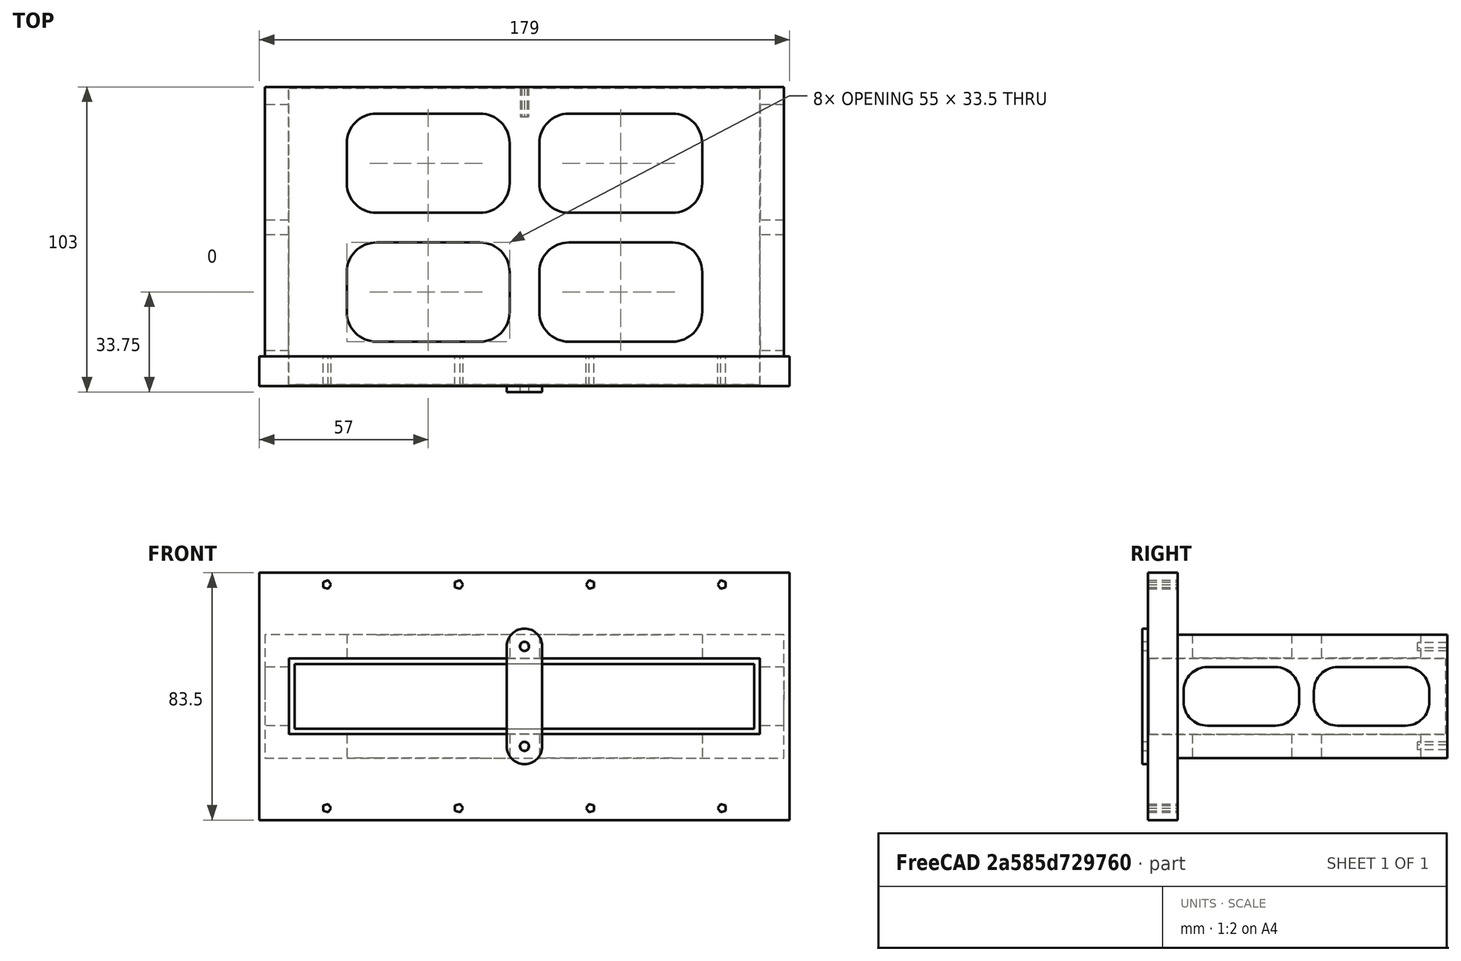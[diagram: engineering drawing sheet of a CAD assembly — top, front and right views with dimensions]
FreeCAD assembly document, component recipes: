
FREECAD ASSEMBLY — COMPONENT RECIPES ("tplink-er605")

This assembly document has 3 components, labeled P0..P2 below (a component is one placed body or linked part). 3 of them carry a construction recipe — the FreeCAD feature program that regenerates the part from scratch, quoted from this document or its linked companion documents; the rest are supplied as boundary geometry only. No exploded tour is included for this assembly.
COMPONENT P0 — recipe-attached ("ER605", modeled in this document).
Construction recipe (the document's own serialized feature program — sketch geometry with constraints, then the solid features built on it; lengths are millimeters unless a unit is written):

FEATURE [PartDesign::Plane] DatumPlane006  label="ER605 Front"
  Length = 176.833
  MapMode = 5
  Placement = pos=(0,0,0) rot=(1,0,0;1.5708rad)
  ResizeMode = 0
  Support = -> [XZ_Plane004]
  Width = 67.8326
FEATURE [PartDesign::Plane] DatumPlane007  label="ER605 Back"
  AttachmentOffset = pos=(0,0,-100.5) rot=(0,0,1;0rad)
  Length = 176.833
  MapMode = 5
  Placement = pos=(0,100.5,2.23e-14) rot=(1,0,0;1.5708rad)
  ResizeMode = 0
  Support = -> [DatumPlane006]
  Width = 67.8326
FEATURE [Sketcher::SketchObject] Sketch008  label="ER605 Front Profile"
  FullyConstrained = true
  MapMode = 5
  Placement = pos=(0,0,0) rot=(1,0,0;1.5708rad)
  Support = -> [DatumPlane006]
  sketch-geometry (5):
    g0: LineSegment StartX=-79.5 StartY=12.75 StartZ=0 EndX=-79.5 EndY=-12.75 EndZ=0
    g1: LineSegment StartX=-79.5 StartY=-12.75 StartZ=0 EndX=79.5 EndY=-12.75 EndZ=0
    g2: LineSegment StartX=79.5 StartY=-12.75 StartZ=0 EndX=79.5 EndY=12.75 EndZ=0
    g3: LineSegment StartX=79.5 StartY=12.75 StartZ=0 EndX=-79.5 EndY=12.75 EndZ=0
    g4: GeomPoint X=0 Y=0 Z=0
  constraints (12):
    c: Coincident(g0,g1)
    c: Coincident(g1,g2)
    c: Coincident(g2,g3)
    c: Coincident(g3,g0)
    c: Horizontal(g1)
    c: Horizontal(g3)
    c: Vertical(g0)
    c: Vertical(g2)
    c: Symmetric(g1,g0,g4)
    c: Coincident(g4,g-1)
    c: DistanceX(g3,g3) = 159  'width'
    c: DistanceY(g2,g2) = 25.5  'height'
FEATURE [PartDesign::Pad] Pad002  label="ER605 Volume"
  Direction = (0,-1,-2e-16)
  Length = 10
  Length2 = 10
  Placement = pos=(0,0,0) rot=(1,0,0;1.5708rad)
  Profile = -> Sketch008
  ReferenceAxis = -> Sketch008 [N_Axis]
  Type = 3
  UpToFace = -> DatumPlane007 [Plane]
FEATURE [PartDesign::Body] ER605_Body  label="ER605 Body"
  Group = -> [DatumPlane006,DatumPlane007,Sketch008,Pad002]
  Origin = -> Origin004
  Tip = -> Pad002
COMPONENT P1 — recipe-attached ("Rack Mount", modeled in this document).
Construction recipe (the document's own serialized feature program — sketch geometry with constraints, then the solid features built on it; lengths are millimeters unless a unit is written):

FEATURE [PartDesign::Plane] DatumPlane  label="Front Panel Front"
  Length = 203.451
  MapMode = 5
  Placement = pos=(0,0,0) rot=(1,0,0;1.5708rad)
  ResizeMode = 0
  Support = -> [XZ_Plane]
  Width = 107.951
FEATURE [PartDesign::Plane] DatumPlane002  label="Front Panel Back"
  AttachmentOffset = pos=(0,0,-10) rot=(0,0,1;0rad)
  Length = 203.451
  MapMode = 5
  Placement = pos=(0,10,2.2e-15) rot=(1,0,0;1.5708rad)
  ResizeMode = 0
  Support = -> [DatumPlane]
  Width = 107.951
FEATURE [Sketcher::SketchObject] Sketch  label="Front Panel Outer"
  FullyConstrained = true
  MapMode = 5
  Placement = pos=(0,0,0) rot=(1,0,0;1.5708rad)
  Support = -> [DatumPlane]
  sketch-geometry (5):
    g0: LineSegment StartX=-89.5 StartY=41.75 StartZ=0 EndX=-89.5 EndY=-41.75 EndZ=0
    g1: LineSegment StartX=-89.5 StartY=-41.75 StartZ=0 EndX=89.5 EndY=-41.75 EndZ=0
    g2: LineSegment StartX=89.5 StartY=-41.75 StartZ=0 EndX=89.5 EndY=41.75 EndZ=0
    g3: LineSegment StartX=89.5 StartY=41.75 StartZ=0 EndX=-89.5 EndY=41.75 EndZ=0
    g4: GeomPoint X=0 Y=0 Z=0
  constraints (12):
    c: Coincident(g0,g1)
    c: Coincident(g1,g2)
    c: Coincident(g2,g3)
    c: Coincident(g3,g0)
    c: Horizontal(g1)
    c: Horizontal(g3)
    c: Vertical(g0)
    c: Vertical(g2)
    c: Symmetric(g1,g0,g4)
    c: Coincident(g4,g-1)
    c: DistanceX(g3,g3) = 179  'width'
    c: DistanceY(g2,g2) = 83.5  'height'
FEATURE [PartDesign::Pad] Pad  label="Front Panel"
  Direction = (0,-1,-2e-16)
  Length = 10
  Length2 = 10
  Placement = pos=(0,0,0) rot=(1,0,0;1.5708rad)
  Profile = -> Sketch
  ReferenceAxis = -> Sketch [N_Axis]
  Type = 3
  UpToFace = -> DatumPlane002 [Plane]
FEATURE [Sketcher::SketchObject] Sketch002  label="Front Panel Mounting Holes Outer"
  FullyConstrained = true
  MapMode = 5
  Placement = pos=(0,0,0) rot=(1,0,0;1.5708rad)
  Support = -> [DatumPlane]
  sketch-geometry (51):
    g0: LineSegment StartX=-66.75 StartY=37.75 StartZ=0 EndX=66.75 EndY=37.75 EndZ=0
    g1: LineSegment StartX=0 StartY=37.75 StartZ=0 EndX=0 EndY=-37.75 EndZ=0
    g2: LineSegment StartX=23.4635 StartY=38.6317 StartZ=0 EndX=21.7865 EndY=39.1766 EndZ=0
    g3: LineSegment StartX=21.7865 StartY=39.1766 StartZ=0 EndX=20.75 EndY=37.75 EndZ=0
    g4: LineSegment StartX=20.75 StartY=37.75 StartZ=0 EndX=21.7865 EndY=36.3234 EndZ=0
    g5: LineSegment StartX=21.7865 StartY=36.3234 StartZ=0 EndX=23.4635 EndY=36.8683 EndZ=0
    g6: LineSegment StartX=23.4635 StartY=36.8683 StartZ=0 EndX=23.4635 EndY=38.6317 EndZ=0
    g7: Circle CenterX=22.25 CenterY=37.75 CenterZ=0 NormalX=0 NormalY=0 NormalZ=1 AngleXU=0 Radius=1.5
    g8: LineSegment StartX=67.9635 StartY=36.8683 StartZ=0 EndX=67.9635 EndY=38.6317 EndZ=0
    g9: LineSegment StartX=67.9635 StartY=38.6317 StartZ=0 EndX=66.2865 EndY=39.1766 EndZ=0
    g10: LineSegment StartX=66.2865 StartY=39.1766 StartZ=0 EndX=65.25 EndY=37.75 EndZ=0
    g11: LineSegment StartX=65.25 StartY=37.75 StartZ=0 EndX=66.2865 EndY=36.3234 EndZ=0
    g12: LineSegment StartX=66.2865 StartY=36.3234 StartZ=0 EndX=67.9635 EndY=36.8683 EndZ=0
    g13: Circle CenterX=66.75 CenterY=37.75 CenterZ=0 NormalX=0 NormalY=0 NormalZ=1 AngleXU=0 Radius=1.5
    g14: LineSegment StartX=-20.75 StartY=37.75 StartZ=0 EndX=-21.7865 EndY=39.1766 EndZ=0
    g15: LineSegment StartX=-21.7865 StartY=39.1766 StartZ=0 EndX=-23.4635 EndY=38.6317 EndZ=0
    g16: LineSegment StartX=-23.4635 StartY=38.6317 StartZ=0 EndX=-23.4635 EndY=36.8683 EndZ=0
    g17: LineSegment StartX=-23.4635 StartY=36.8683 StartZ=0 EndX=-21.7865 EndY=36.3234 EndZ=0
    g18: LineSegment StartX=-21.7865 StartY=36.3234 StartZ=0 EndX=-20.75 EndY=37.75 EndZ=0
    g19: Circle CenterX=-22.25 CenterY=37.75 CenterZ=0 NormalX=0 NormalY=0 NormalZ=1 AngleXU=0 Radius=1.5
    g20: LineSegment StartX=-65.25 StartY=37.75 StartZ=0 EndX=-66.2865 EndY=39.1766 EndZ=0
    g21: LineSegment StartX=-66.2865 StartY=39.1766 StartZ=0 EndX=-67.9635 EndY=38.6317 EndZ=0
    g22: LineSegment StartX=-67.9635 StartY=38.6317 StartZ=0 EndX=-67.9635 EndY=36.8683 EndZ=0
    g23: LineSegment StartX=-67.9635 StartY=36.8683 StartZ=0 EndX=-66.2865 EndY=36.3234 EndZ=0
    g24: LineSegment StartX=-66.2865 StartY=36.3234 StartZ=0 EndX=-65.25 EndY=37.75 EndZ=0
    g25: Circle CenterX=-66.75 CenterY=37.75 CenterZ=0 NormalX=0 NormalY=0 NormalZ=1 AngleXU=0 Radius=1.5
    g26: LineSegment StartX=-66.2865 StartY=-39.1766 StartZ=0 EndX=-65.25 EndY=-37.75 EndZ=0
    g27: LineSegment StartX=-65.25 StartY=-37.75 StartZ=0 EndX=-66.2865 EndY=-36.3234 EndZ=0
    g28: LineSegment StartX=-66.2865 StartY=-36.3234 StartZ=0 EndX=-67.9635 EndY=-36.8683 EndZ=0
    g29: LineSegment StartX=-67.9635 StartY=-36.8683 StartZ=0 EndX=-67.9635 EndY=-38.6317 EndZ=0
    g30: LineSegment StartX=-67.9635 StartY=-38.6317 StartZ=0 EndX=-66.2865 EndY=-39.1766 EndZ=0
    g31: Circle CenterX=-66.75 CenterY=-37.75 CenterZ=0 NormalX=0 NormalY=0 NormalZ=1 AngleXU=0 Radius=1.5
    g32: LineSegment StartX=-20.75 StartY=-37.75 StartZ=0 EndX=-21.7865 EndY=-36.3234 EndZ=0
    g33: LineSegment StartX=-21.7865 StartY=-36.3234 StartZ=0 EndX=-23.4635 EndY=-36.8683 EndZ=0
    g34: LineSegment StartX=-23.4635 StartY=-36.8683 StartZ=0 EndX=-23.4635 EndY=-38.6317 EndZ=0
    g35: LineSegment StartX=-23.4635 StartY=-38.6317 StartZ=0 EndX=-21.7865 EndY=-39.1766 EndZ=0
    g36: LineSegment StartX=-21.7865 StartY=-39.1766 StartZ=0 EndX=-20.75 EndY=-37.75 EndZ=0
    g37: Circle CenterX=-22.25 CenterY=-37.75 CenterZ=0 NormalX=0 NormalY=0 NormalZ=1 AngleXU=0 Radius=1.5
    g38: LineSegment StartX=21.7865 StartY=-39.1766 StartZ=0 EndX=23.4635 EndY=-38.6317 EndZ=0
    g39: LineSegment StartX=23.4635 StartY=-38.6317 StartZ=0 EndX=23.4635 EndY=-36.8683 EndZ=0
    g40: LineSegment StartX=23.4635 StartY=-36.8683 StartZ=0 EndX=21.7865 EndY=-36.3234 EndZ=0
    g41: LineSegment StartX=21.7865 StartY=-36.3234 StartZ=0 EndX=20.75 EndY=-37.75 EndZ=0
    g42: LineSegment StartX=20.75 StartY=-37.75 StartZ=0 EndX=21.7865 EndY=-39.1766 EndZ=0
    g43: Circle CenterX=22.25 CenterY=-37.75 CenterZ=0 NormalX=0 NormalY=0 NormalZ=1 AngleXU=0 Radius=1.5
    g44: LineSegment StartX=67.9635 StartY=-36.8683 StartZ=0 EndX=66.2865 EndY=-36.3234 EndZ=0
    g45: LineSegment StartX=66.2865 StartY=-36.3234 StartZ=0 EndX=65.25 EndY=-37.75 EndZ=0
    g46: LineSegment StartX=65.25 StartY=-37.75 StartZ=0 EndX=66.2865 EndY=-39.1766 EndZ=0
    g47: LineSegment StartX=66.2865 StartY=-39.1766 StartZ=0 EndX=67.9635 EndY=-38.6317 EndZ=0
    g48: LineSegment StartX=67.9635 StartY=-38.6317 StartZ=0 EndX=67.9635 EndY=-36.8683 EndZ=0
    g49: Circle CenterX=66.75 CenterY=-37.75 CenterZ=0 NormalX=0 NormalY=0 NormalZ=1 AngleXU=0 Radius=1.5
    g50: LineSegment StartX=-66.75 StartY=-37.75 StartZ=0 EndX=66.75 EndY=-37.75 EndZ=0
  constraints (122):
    c: Horizontal(g0)
    c: PointOnObject(g1,g-2)
    c: Symmetric(g1,g1,g-1)
    c: DistanceY(g1,g1) = 75.5
    c: Symmetric(g0,g0,g1)
    c: Coincident(g2,g3)
    c: Coincident(g3,g4)
    c: Coincident(g4,g5)
    c: Coincident(g5,g6)
    c: Coincident(g6,g2)
    c: Equal(g2, g3-g6) x4
    c: PointOnObject(g2,g7)
    c: PointOnObject(g3,g7)
    c: PointOnObject(g4,g7)
    c: PointOnObject(g5,g7)
    c: PointOnObject(g6,g7)
    c: PointOnObject(g7,g0)
    c: Coincident(g8,g9)
    c: Coincident(g9,g10)
    c: Coincident(g10,g11)
    c: Coincident(g11,g12)
    c: Coincident(g12,g8)
    c: Equal(g8, g9-g12) x4
    c: PointOnObject(g8,g13)
    c: PointOnObject(g9,g13)
    c: PointOnObject(g10,g13)
    c: PointOnObject(g11,g13)
    c: PointOnObject(g12,g13)
    c: Coincident(g13,g0)
    c: Coincident(g14,g15)
    c: Coincident(g15,g16)
    c: Coincident(g16,g17)
    c: Coincident(g17,g18)
    c: Coincident(g18,g14)
    c: Equal(g14, g15-g18) x4
    c: PointOnObject(g14,g19)
    c: PointOnObject(g15,g19)
    c: PointOnObject(g16,g19)
    c: PointOnObject(g17,g19)
    c: PointOnObject(g18,g19)
    c: PointOnObject(g19,g0)
    c: Coincident(g20,g21)
    c: Coincident(g21,g22)
    c: Coincident(g22,g23)
    c: Coincident(g23,g24)
    c: Coincident(g24,g20)
    c: Equal(g20, g21-g24) x4
    c: PointOnObject(g20,g25)
    c: PointOnObject(g21,g25)
    c: PointOnObject(g22,g25)
    c: PointOnObject(g23,g25)
    c: PointOnObject(g24,g25)
    c: Coincident(g25,g0)
    c: DistanceX(g7,g0) = 44.5
    c: Equal(g7,g13)
    c: Equal(g19,g25)
    c: Coincident(g26,g27)
    c: Coincident(g27,g28)
    c: Coincident(g28,g29)
    c: Coincident(g29,g30)
    c: Coincident(g30,g26)
    c: Equal(g26, g27-g30) x4
    c: PointOnObject(g26,g31)
    c: PointOnObject(g27,g31)
    c: PointOnObject(g28,g31)
    c: PointOnObject(g29,g31)
    c: PointOnObject(g30,g31)
    c: Coincident(g32,g33)
    c: Coincident(g33,g34)
    c: Coincident(g34,g35)
    c: Coincident(g35,g36)
    c: Coincident(g36,g32)
    c: Equal(g32, g33-g36) x4
    c: PointOnObject(g32,g37)
    c: PointOnObject(g33,g37)
    c: PointOnObject(g34,g37)
    c: PointOnObject(g35,g37)
    c: PointOnObject(g36,g37)
    c: Coincident(g38,g39)
    c: Coincident(g39,g40)
    c: Coincident(g40,g41)
    c: Coincident(g41,g42)
    c: Coincident(g42,g38)
    c: Equal(g38, g39-g42) x4
    c: PointOnObject(g38,g43)
    c: PointOnObject(g39,g43)
    c: PointOnObject(g40,g43)
    c: PointOnObject(g41,g43)
    c: PointOnObject(g42,g43)
    c: Coincident(g44,g45)
    c: Coincident(g45,g46)
    c: Coincident(g46,g47)
    c: Coincident(g47,g48)
    c: Coincident(g48,g44)
    c: Equal(g44, g45-g48) x4
    c: PointOnObject(g44,g49)
    c: PointOnObject(g45,g49)
    c: PointOnObject(g46,g49)
    c: PointOnObject(g47,g49)
    c: PointOnObject(g48,g49)
    c: Symmetric(g19,g37,g-1)
    c: Symmetric(g31,g0,g-1)
    c: Symmetric(g7,g43,g-1)
    c: Symmetric(g0,g49,g-1)
    c: Equal(g31,g37)
    c: Diameter(g13) = 3
    c: Equal(g31,g13)
    c: PointOnObject(g10,g0)
    c: PointOnObject(g3,g0)
    c: PointOnObject(g14,g0)
    c: PointOnObject(g20,g0)
    c: Coincident(g50,g31)
    c: Coincident(g50,g49)
    c: PointOnObject(g45,g50)
    c: PointOnObject(g41,g50)
    c: PointOnObject(g32,g50)
    c: PointOnObject(g26,g50)
    c: Equal(g19,g7)
    c: Equal(g13,g49)
    c: Equal(g49,g43)
    c: DistanceX(g19,g7) = 44.5
    c: DistanceX(g0,g19) = 44.5
FEATURE [PartDesign::Pocket] Pocket001  label="Front Panel Mounting Holes"
  BaseFeature = -> Pad
  Direction = (0,1,2e-16)
  Length = 0
  Length2 = 5
  Placement = pos=(0,0,0) rot=(1,0,0;1.5708rad)
  Profile = -> Sketch002
  ReferenceAxis = -> Sketch002 [N_Axis]
  Type = 3
  UpToFace = -> DatumPlane002
FEATURE [Sketcher::SketchObject] Sketch003  label="Front Panel Cutout Outer"
  FullyConstrained = true
  MapMode = 5
  Placement = pos=(0,0,0) rot=(1,0,0;1.5708rad)
  Support = -> [DatumPlane]
  expr: Constraints[10] = <<Device Cutout Outer>>.Constraints.height - 4 mm
  expr: Constraints[11] = <<Device Cutout Outer>>.Constraints.width - 4 mm
  sketch-geometry (5):
    g0: LineSegment StartX=-77.625 StartY=10.875 StartZ=0 EndX=-77.625 EndY=-10.875 EndZ=0
    g1: LineSegment StartX=-77.625 StartY=-10.875 StartZ=0 EndX=77.625 EndY=-10.875 EndZ=0
    g2: LineSegment StartX=77.625 StartY=-10.875 StartZ=0 EndX=77.625 EndY=10.875 EndZ=0
    g3: LineSegment StartX=77.625 StartY=10.875 StartZ=0 EndX=-77.625 EndY=10.875 EndZ=0
    g4: GeomPoint X=0 Y=0 Z=0
  constraints (12):
    c: Coincident(g0,g1)
    c: Coincident(g1,g2)
    c: Coincident(g2,g3)
    c: Coincident(g3,g0)
    c: Horizontal(g1)
    c: Horizontal(g3)
    c: Vertical(g0)
    c: Vertical(g2)
    c: Symmetric(g1,g0,g4)
    c: Coincident(g4,g-1)
    c: DistanceY(g2,g2) = 21.75
    c: DistanceX(g3,g3) = 155.25
FEATURE [PartDesign::Pocket] Pocket  label="Front Panel Cutout"
  BaseFeature = -> Pocket001
  Direction = (0,1,2e-16)
  Length = 0
  Length2 = 5
  Placement = pos=(0,0,0) rot=(1,0,0;1.5708rad)
  Profile = -> Sketch003
  ReferenceAxis = -> Sketch003 [N_Axis]
  Type = 3
  UpToFace = -> DatumPlane002
FEATURE [PartDesign::Plane] DatumPlane003  label="Front Side Of Device"
  AttachmentOffset = pos=(0,0,-0.5) rot=(0,0,1;0rad)
  Length = 203.451
  MapMode = 5
  Placement = pos=(0,0.5,1e-16) rot=(1,0,0;1.5708rad)
  ResizeMode = 0
  Support = -> [DatumPlane]
  Width = 107.951
FEATURE [Sketcher::SketchObject] Sketch004  label="Device Cutout Outer"
  FullyConstrained = true
  MapMode = 5
  Placement = pos=(0,0.5,1e-16) rot=(1,0,0;1.5708rad)
  Support = -> [DatumPlane003]
  expr: .Constraints.height = <<ER605 Front Profile>>.Constraints.height + 0.25 mm
  expr: .Constraints.width = <<ER605 Front Profile>>.Constraints.width + 0.25 mm
  sketch-geometry (5):
    g0: LineSegment StartX=-79.625 StartY=-12.875 StartZ=0 EndX=-79.625 EndY=12.875 EndZ=0
    g1: LineSegment StartX=-79.625 StartY=12.875 StartZ=0 EndX=79.625 EndY=12.875 EndZ=0
    g2: LineSegment StartX=79.625 StartY=12.875 StartZ=0 EndX=79.625 EndY=-12.875 EndZ=0
    g3: LineSegment StartX=79.625 StartY=-12.875 StartZ=0 EndX=-79.625 EndY=-12.875 EndZ=0
    g4: GeomPoint X=0 Y=0 Z=0
  constraints (12):
    c: Coincident(g0,g1)
    c: Coincident(g1,g2)
    c: Coincident(g2,g3)
    c: Coincident(g3,g0)
    c: Horizontal(g1)
    c: Horizontal(g3)
    c: Vertical(g0)
    c: Vertical(g2)
    c: Symmetric(g1,g0,g4)
    c: Coincident(g4,g-1)
    c: DistanceY(g2,g2) = 25.75  'height'
    c: DistanceX(g1,g1) = 159.25  'width'
FEATURE [PartDesign::Plane] DatumPlane004  label="Back Side Of Device"
  AttachmentOffset = pos=(0,0,-100.5) rot=(0,0,1;0rad)
  Length = 203.451
  MapMode = 5
  Placement = pos=(0,101,2.24e-14) rot=(1,0,0;1.5708rad)
  ResizeMode = 0
  Support = -> [DatumPlane003]
  Width = 107.951
FEATURE [Sketcher::SketchObject] Sketch005  label="Device Shelf Outer"
  FullyConstrained = true
  MapMode = 5
  Placement = pos=(0,0.5,1e-16) rot=(1,0,0;1.5708rad)
  Support = -> [DatumPlane003]
  expr: .Constraints.height = <<Device Cutout Outer>>.Constraints.height + 16 mm
  expr: .Constraints.width = <<Device Cutout Outer>>.Constraints.width + 16 mm
  sketch-geometry (5):
    g0: LineSegment StartX=-87.625 StartY=20.875 StartZ=0 EndX=-87.625 EndY=-20.875 EndZ=0
    g1: LineSegment StartX=-87.625 StartY=-20.875 StartZ=0 EndX=87.625 EndY=-20.875 EndZ=0
    g2: LineSegment StartX=87.625 StartY=-20.875 StartZ=0 EndX=87.625 EndY=20.875 EndZ=0
    g3: LineSegment StartX=87.625 StartY=20.875 StartZ=0 EndX=-87.625 EndY=20.875 EndZ=0
    g4: GeomPoint X=0 Y=0 Z=0
  constraints (12):
    c: Coincident(g0,g1)
    c: Coincident(g1,g2)
    c: Coincident(g2,g3)
    c: Coincident(g3,g0)
    c: Horizontal(g1)
    c: Horizontal(g3)
    c: Vertical(g0)
    c: Vertical(g2)
    c: Symmetric(g1,g0,g4)
    c: DistanceX(g3,g3) = 175.25  'width'
    c: Coincident(g4,g-1)
    c: DistanceY(g2,g2) = 41.75  'height'
FEATURE [PartDesign::Pad] Pad001  label="Device Shelf"
  BaseFeature = -> Pocket
  Direction = (0,-1,-2e-16)
  Length = 10
  Length2 = 10
  Placement = pos=(0,0,0) rot=(1,0,0;1.5708rad)
  Profile = -> Sketch005
  ReferenceAxis = -> Sketch005 [N_Axis]
  Type = 3
  UpToFace = -> DatumPlane004
FEATURE [PartDesign::Pocket] Pocket002  label="Device Cutout"
  BaseFeature = -> Pad001
  Direction = (0,1,2e-16)
  Length = 0
  Length2 = 5
  Placement = pos=(0,0,0) rot=(1,0,0;1.5708rad)
  Profile = -> Sketch004
  ReferenceAxis = -> Sketch004 [N_Axis]
  Type = 3
  UpToFace = -> DatumPlane004 [Plane]
FEATURE [PartDesign::Plane] DatumPlane008  label="Device Shelf Top"
  AttachmentOffset = pos=(0,0,20.875) rot=(0,0,1;0rad)
  Length = 209.036
  MapMode = 5
  Placement = pos=(0,0,20.875) rot=(0,0,1;0rad)
  ResizeMode = 0
  Support = -> [XY_Plane]
  Width = 156.036
  expr: .AttachmentOffset.Base.z = <<Device Shelf Outer>>.Constraints.height / 2
FEATURE [Sketcher::SketchObject] Sketch006  label="Vents Top Bottom Shape"
  FullyConstrained = true
  MapMode = 5
  Placement = pos=(0,0,20.875) rot=(0,0,1;0rad)
  Support = -> [DatumPlane008]
  sketch-geometry (40):
    g0: ArcOfCircle CenterX=-50 CenterY=82 CenterZ=0 NormalX=0 NormalY=0 NormalZ=1 AngleXU=0 Radius=10 StartAngle=1.5708 EndAngle=3.14159
    g1: LineSegment StartX=-50 StartY=92 StartZ=0 EndX=-15 EndY=92 EndZ=0
    g2: ArcOfCircle CenterX=-15 CenterY=82 CenterZ=0 NormalX=0 NormalY=0 NormalZ=1 AngleXU=0 Radius=10 StartAngle=6e-16 EndAngle=1.5708
    g3: LineSegment StartX=-5 StartY=82 StartZ=0 EndX=-5 EndY=68.5 EndZ=0
    g4: ArcOfCircle CenterX=-15 CenterY=68.5 CenterZ=0 NormalX=0 NormalY=0 NormalZ=1 AngleXU=0 Radius=10 StartAngle=4.71239 EndAngle=6.28319
    g5: LineSegment StartX=-15 StartY=58.5 StartZ=0 EndX=-50 EndY=58.5 EndZ=0
    g6: ArcOfCircle CenterX=-50 CenterY=68.5 CenterZ=0 NormalX=0 NormalY=0 NormalZ=1 AngleXU=0 Radius=10 StartAngle=3.14159 EndAngle=4.71239
    g7: LineSegment StartX=-60 StartY=68.5 StartZ=0 EndX=-60 EndY=82 EndZ=0
    g8: GeomPoint X=-60 Y=92 Z=0
    g9: GeomPoint X=-5 Y=58.5 Z=0
    g10: ArcOfCircle CenterX=15 CenterY=82 CenterZ=0 NormalX=0 NormalY=0 NormalZ=1 AngleXU=0 Radius=10 StartAngle=1.5708 EndAngle=3.14159
    g11: LineSegment StartX=15 StartY=92 StartZ=0 EndX=50 EndY=92 EndZ=0
    g12: ArcOfCircle CenterX=50 CenterY=82 CenterZ=0 NormalX=0 NormalY=0 NormalZ=1 AngleXU=0 Radius=10 StartAngle=-8.145e-13 EndAngle=1.5708
    g13: LineSegment StartX=60 StartY=82 StartZ=0 EndX=60 EndY=68.5 EndZ=0
    g14: ArcOfCircle CenterX=50 CenterY=68.5 CenterZ=0 NormalX=0 NormalY=0 NormalZ=1 AngleXU=0 Radius=10 StartAngle=4.71239 EndAngle=6.28319
    g15: LineSegment StartX=50 StartY=58.5 StartZ=0 EndX=15 EndY=58.5 EndZ=0
    g16: ArcOfCircle CenterX=15 CenterY=68.5 CenterZ=0 NormalX=0 NormalY=0 NormalZ=1 AngleXU=0 Radius=10 StartAngle=3.14159 EndAngle=4.71239
    g17: LineSegment StartX=5 StartY=68.5 StartZ=0 EndX=5 EndY=82 EndZ=0
    g18: GeomPoint X=5 Y=92 Z=0
    g19: GeomPoint X=60 Y=58.5 Z=0
    g20: ArcOfCircle CenterX=-50 CenterY=38.5 CenterZ=0 NormalX=0 NormalY=0 NormalZ=1 AngleXU=0 Radius=10 StartAngle=1.5708 EndAngle=3.14159
    g21: LineSegment StartX=-50 StartY=48.5 StartZ=0 EndX=-15 EndY=48.5 EndZ=0
    g22: ArcOfCircle CenterX=-15 CenterY=38.5 CenterZ=0 NormalX=0 NormalY=0 NormalZ=1 AngleXU=0 Radius=10 StartAngle=4e-16 EndAngle=1.5708
    g23: LineSegment StartX=-5 StartY=38.5 StartZ=0 EndX=-5 EndY=25 EndZ=0
    g24: ArcOfCircle CenterX=-15 CenterY=25 CenterZ=0 NormalX=0 NormalY=0 NormalZ=1 AngleXU=0 Radius=10 StartAngle=4.71239 EndAngle=6.28319
    g25: LineSegment StartX=-15 StartY=15 StartZ=0 EndX=-50 EndY=15 EndZ=0
    g26: ArcOfCircle CenterX=-50 CenterY=25 CenterZ=0 NormalX=0 NormalY=0 NormalZ=1 AngleXU=0 Radius=10 StartAngle=3.14159 EndAngle=4.71239
    g27: LineSegment StartX=-60 StartY=25 StartZ=0 EndX=-60 EndY=38.5 EndZ=0
    g28: GeomPoint X=-60 Y=48.5 Z=0
    g29: GeomPoint X=-5 Y=15 Z=0
    g30: ArcOfCircle CenterX=15 CenterY=38.5 CenterZ=0 NormalX=0 NormalY=0 NormalZ=1 AngleXU=0 Radius=10 StartAngle=1.5708 EndAngle=3.14159
    g31: LineSegment StartX=15 StartY=48.5 StartZ=0 EndX=50 EndY=48.5 EndZ=0
    g32: ArcOfCircle CenterX=50 CenterY=38.5 CenterZ=0 NormalX=0 NormalY=0 NormalZ=1 AngleXU=0 Radius=10 StartAngle=2e-16 EndAngle=1.5708
    g33: LineSegment StartX=60 StartY=38.5 StartZ=0 EndX=60 EndY=25 EndZ=0
    g34: ArcOfCircle CenterX=50 CenterY=25 CenterZ=0 NormalX=0 NormalY=0 NormalZ=1 AngleXU=0 Radius=10 StartAngle=4.71239 EndAngle=6.28319
    g35: LineSegment StartX=50 StartY=15 StartZ=0 EndX=15 EndY=15 EndZ=0
    g36: ArcOfCircle CenterX=15 CenterY=25 CenterZ=0 NormalX=0 NormalY=0 NormalZ=1 AngleXU=0 Radius=10 StartAngle=3.14159 EndAngle=4.71239
    g37: LineSegment StartX=5 StartY=25 StartZ=0 EndX=5 EndY=38.5 EndZ=0
    g38: GeomPoint X=5 Y=48.5 Z=0
    g39: GeomPoint X=60 Y=15 Z=0
  constraints (95):
    c: Tangent(g0,g1) = 1.5708
    c: Tangent(g1,g2) = 1.5708
    c: Tangent(g2,g3) = 1.5708
    c: Tangent(g3,g4) = 1.5708
    c: Tangent(g4,g5) = 1.5708
    c: Tangent(g5,g6) = 1.5708
    c: Tangent(g6,g7) = 1.5708
    c: Tangent(g7,g0) = 1.5708
    c: Horizontal(g1)
    c: Horizontal(g5)
    c: Vertical(g3)
    c: Vertical(g7)
    c: Equal(g0,g2)
    c: Equal(g2,g4)
    c: Equal(g4,g6)
    c: PointOnObject(g8,g1)
    c: PointOnObject(g8,g7)
    c: PointOnObject(g9,g3)
    c: PointOnObject(g9,g5)
    c: Tangent(g10,g11) = 1.5708
    c: Tangent(g11,g12) = 1.5708
    c: Tangent(g12,g13) = 1.5708
    c: Tangent(g13,g14) = 1.5708
    c: Tangent(g14,g15) = 1.5708
    c: Tangent(g15,g16) = 1.5708
    c: Tangent(g16,g17) = 1.5708
    c: Tangent(g17,g10) = 1.5708
    c: Horizontal(g11)
    c: Horizontal(g15)
    c: Vertical(g13)
    c: Vertical(g17)
    c: Equal(g10,g12)
    c: Equal(g12,g14)
    c: Equal(g14,g16)
    c: PointOnObject(g18,g11)
    c: PointOnObject(g18,g17)
    c: PointOnObject(g19,g13)
    c: PointOnObject(g19,g15)
    c: Tangent(g20,g21) = 1.5708
    c: Tangent(g21,g22) = 1.5708
    c: Tangent(g22,g23) = 1.5708
    c: Tangent(g23,g24) = 1.5708
    c: Tangent(g24,g25) = 1.5708
    c: Tangent(g25,g26) = 1.5708
    c: Tangent(g26,g27) = 1.5708
    c: Tangent(g27,g20) = 1.5708
    c: Horizontal(g21)
    c: Horizontal(g25)
    c: Vertical(g23)
    c: Vertical(g27)
    c: Equal(g20,g22)
    c: Equal(g22,g24)
    c: Equal(g24,g26)
    c: PointOnObject(g28,g21)
    c: PointOnObject(g28,g27)
    c: PointOnObject(g29,g23)
    c: PointOnObject(g29,g25)
    c: Tangent(g30,g31) = 1.5708
    c: Tangent(g31,g32) = 1.5708
    c: Tangent(g32,g33) = 1.5708
    c: Tangent(g33,g34) = 1.5708
    c: Tangent(g34,g35) = 1.5708
    c: Tangent(g35,g36) = 1.5708
    c: Tangent(g36,g37) = 1.5708
    c: Tangent(g37,g30) = 1.5708
    c: Horizontal(g31)
    c: Horizontal(g35)
    c: Vertical(g33)
    c: Vertical(g37)
    c: Equal(g30,g32)
    c: Equal(g32,g34)
    c: Equal(g34,g36)
    c: PointOnObject(g38,g31)
    c: PointOnObject(g38,g37)
    c: PointOnObject(g39,g33)
    c: PointOnObject(g39,g35)
    c: Equal(g2,g22)
    c: Equal(g22,g12)
    c: Equal(g12,g32)
    c: Equal(g21,g1)
    c: Equal(g1,g11)
    c: Equal(g11,g31)
    c: Equal(g3,g23)
    c: Equal(g23,g33)
    c: Equal(g33,g13)
    c: Vertical(g6,g26)
    c: Vertical(g16,g36)
    c: Horizontal(g16,g6)
    c: Radius(g12) = 10
    c: Symmetric(g23,g36,g-2)
    c: DistanceY(g-1,g34) = 15
    c: DistanceY(g-1,g11) = 92
    c: DistanceY(g20,g5) = 10
    c: DistanceX(g2,g10) = 10
    c: DistanceX(g0,g12) = 120
FEATURE [PartDesign::Plane] DatumPlane009  label="Device Shelf Bottom"
  AttachmentOffset = pos=(0,0,-20.875) rot=(0,0,1;0rad)
  Length = 209.036
  MapMode = 5
  Placement = pos=(0,0,-20.875) rot=(0,0,1;0rad)
  ResizeMode = 0
  Support = -> [XY_Plane]
  Width = 156.036
  expr: .AttachmentOffset.Base.z = -<<Device Shelf Outer>>.Constraints.height / 2
FEATURE [PartDesign::Pocket] Pocket003  label="Vents Top Bottom"
  BaseFeature = -> Pocket002
  Direction = (0,0,-1)
  Length = 0
  Length2 = 5
  Placement = pos=(0,0,0) rot=(1,0,0;1.5708rad)
  Profile = -> Sketch006
  ReferenceAxis = -> Sketch006 [N_Axis]
  Type = 3
  UpToFace = -> DatumPlane009 [Plane]
FEATURE [PartDesign::Plane] DatumPlane010  label="Device Shelf Right"
  AttachmentOffset = pos=(0,0,87.625) rot=(0,0,1;0rad)
  Length = 146.514
  MapMode = 5
  Placement = pos=(87.625,-1.95e-14,1.95e-14) rot=(0.57735,0.57735,0.57735;2.0944rad)
  ResizeMode = 0
  Support = -> [YZ_Plane]
  Width = 104.014
  expr: .AttachmentOffset.Base.z = <<Device Shelf Outer>>.Constraints.width / 2
FEATURE [Sketcher::SketchObject] Sketch007  label="Vents Left Right Shape"
  FullyConstrained = true
  MapMode = 5
  Placement = pos=(87.625,-1.95e-14,1.95e-14) rot=(0.57735,0.57735,0.57735;2.0944rad)
  Support = -> [DatumPlane010]
  expr: Constraints[41] = <<Device Cutout Outer>>.Constraints.height - 6 mm
  sketch-geometry (20):
    g0: ArcOfCircle CenterX=20 CenterY=1.875 CenterZ=0 NormalX=0 NormalY=0 NormalZ=1 AngleXU=0 Radius=8 StartAngle=1.5708 EndAngle=3.14159
    g1: LineSegment StartX=20 StartY=9.875 StartZ=0 EndX=43 EndY=9.875 EndZ=0
    g2: ArcOfCircle CenterX=43 CenterY=1.875 CenterZ=0 NormalX=0 NormalY=0 NormalZ=1 AngleXU=0 Radius=8 StartAngle=1e-16 EndAngle=1.5708
    g3: LineSegment StartX=51 StartY=1.875 StartZ=0 EndX=51 EndY=-1.875 EndZ=0
    g4: ArcOfCircle CenterX=43 CenterY=-1.875 CenterZ=0 NormalX=0 NormalY=0 NormalZ=1 AngleXU=0 Radius=8 StartAngle=4.71239 EndAngle=6.28319
    g5: LineSegment StartX=43 StartY=-9.875 StartZ=0 EndX=20 EndY=-9.875 EndZ=0
    g6: ArcOfCircle CenterX=20 CenterY=-1.875 CenterZ=0 NormalX=0 NormalY=0 NormalZ=1 AngleXU=0 Radius=8 StartAngle=3.14159 EndAngle=4.71239
    g7: LineSegment StartX=12 StartY=-1.875 StartZ=0 EndX=12 EndY=1.875 EndZ=0
    g8: GeomPoint X=12 Y=9.875 Z=0
    g9: GeomPoint X=51 Y=-9.875 Z=0
    g10: ArcOfCircle CenterX=64 CenterY=1.875 CenterZ=0 NormalX=0 NormalY=0 NormalZ=1 AngleXU=0 Radius=8 StartAngle=1.5708 EndAngle=3.14159
    g11: LineSegment StartX=64 StartY=9.875 StartZ=0 EndX=87 EndY=9.875 EndZ=0
    g12: ArcOfCircle CenterX=87 CenterY=1.875 CenterZ=0 NormalX=0 NormalY=0 NormalZ=1 AngleXU=0 Radius=8 StartAngle=1e-16 EndAngle=1.5708
    g13: LineSegment StartX=95 StartY=1.875 StartZ=0 EndX=95 EndY=-1.875 EndZ=0
    g14: ArcOfCircle CenterX=87 CenterY=-1.875 CenterZ=0 NormalX=0 NormalY=0 NormalZ=1 AngleXU=0 Radius=8 StartAngle=4.71239 EndAngle=6.28319
    g15: LineSegment StartX=87 StartY=-9.875 StartZ=0 EndX=64 EndY=-9.875 EndZ=0
    g16: ArcOfCircle CenterX=64 CenterY=-1.875 CenterZ=0 NormalX=0 NormalY=0 NormalZ=1 AngleXU=0 Radius=8 StartAngle=3.14159 EndAngle=4.71239
    g17: LineSegment StartX=56 StartY=-1.875 StartZ=0 EndX=56 EndY=1.875 EndZ=0
    g18: GeomPoint X=56 Y=9.875 Z=0
    g19: GeomPoint X=95 Y=-9.875 Z=0
  constraints (47):
    c: Tangent(g0,g1) = 1.5708
    c: Tangent(g1,g2) = 1.5708
    c: Tangent(g2,g3) = 1.5708
    c: Tangent(g3,g4) = 1.5708
    c: Tangent(g4,g5) = 1.5708
    c: Tangent(g5,g6) = 1.5708
    c: Tangent(g6,g7) = 1.5708
    c: Tangent(g7,g0) = 1.5708
    c: Horizontal(g1)
    c: Horizontal(g5)
    c: Vertical(g3)
    c: Vertical(g7)
    c: Equal(g0,g2)
    c: Equal(g2,g4)
    c: PointOnObject(g8,g1)
    c: PointOnObject(g8,g7)
    c: PointOnObject(g9,g3)
    c: PointOnObject(g9,g5)
    c: Tangent(g10,g11) = 1.5708
    c: Tangent(g11,g12) = 1.5708
    c: Tangent(g12,g13) = 1.5708
    c: Tangent(g13,g14) = 1.5708
    c: Tangent(g14,g15) = 1.5708
    c: Tangent(g15,g16) = 1.5708
    c: Tangent(g16,g17) = 1.5708
    c: Tangent(g17,g10) = 1.5708
    c: Horizontal(g11)
    c: Horizontal(g15)
    c: Vertical(g13)
    c: Vertical(g17)
    c: Equal(g10,g12)
    c: Equal(g12,g14)
    c: Equal(g14,g16)
    c: PointOnObject(g18,g11)
    c: PointOnObject(g18,g17)
    c: PointOnObject(g19,g13)
    c: PointOnObject(g19,g15)
    c: Symmetric(g0,g6,g-1)
    c: Horizontal(g0,g10)
    c: Horizontal(g6,g16)
    c: Equal(g0,g10)
    c: DistanceY(g5,g0) = 19.75
    c: Equal(g1,g11)
    c: DistanceX(g-1,g6) = 12
    c: DistanceX(g3,g16) = 5
    c: DistanceX(g-1,g13) = 95
    c: Radius(g12) = 8
FEATURE [PartDesign::Plane] DatumPlane011  label="Device Shelf Left"
  AttachmentOffset = pos=(0,0,-87.625) rot=(0,0,1;0rad)
  Length = 146.514
  MapMode = 5
  Placement = pos=(-87.625,1.95e-14,-1.95e-14) rot=(0.57735,0.57735,0.57735;2.0944rad)
  ResizeMode = 0
  Support = -> [YZ_Plane]
  Width = 104.014
  expr: .AttachmentOffset.Base.z = -<<Device Shelf Outer>>.Constraints.width / 2
FEATURE [PartDesign::Pocket] Pocket004  label="Vents Left Right"
  BaseFeature = -> Pocket003
  Direction = (-1,1e-16,-1e-16)
  Length = 0
  Length2 = 5
  Placement = pos=(0,0,0) rot=(1,0,0;1.5708rad)
  Profile = -> Sketch007
  ReferenceAxis = -> Sketch007 [N_Axis]
  Type = 3
  UpToFace = -> DatumPlane011 [Plane]
FEATURE [PartDesign::CoordinateSystem] Local_CS  label="Front Of Device (Body)"
  AttacherType = Attacher::AttachEngine3D
  AttachmentOffset = pos=(0,0,0) rot=(-1,0,0;1.5708rad)
  MapMode = 5
  Placement = pos=(0,0.5,1e-16) rot=(0,0,1;0rad)
  Support = -> [DatumPlane003]
FEATURE [PartDesign::Plane] DatumPlane014  label="Shelf Retention Clamp Mounting Holes Depth"
  AttachmentOffset = pos=(0,0,10) rot=(0,0,1;0rad)
  Length = 203.451
  MapMode = 5
  Placement = pos=(0,91,2.02e-14) rot=(1,0,0;1.5708rad)
  ResizeMode = 0
  Support = -> [DatumPlane004]
  Width = 107.951
FEATURE [Sketcher::SketchObject] Sketch011  label="Shelf Retention Clamp Mounting Holes Outer"
  FullyConstrained = true
  MapMode = 5
  Placement = pos=(0,101,2.24e-14) rot=(1,0,0;1.5708rad)
  Support = -> [DatumPlane004]
  expr: .Constraints.offset = <<Device Shelf Outer>>.Constraints.height - 8 mm
  sketch-geometry (12):
    g0: LineSegment StartX=0 StartY=15.375 StartZ=0 EndX=1.42658 EndY=16.4115 EndZ=0
    g1: LineSegment StartX=1.42658 StartY=16.4115 StartZ=0 EndX=0.881678 EndY=18.0885 EndZ=0
    g2: LineSegment StartX=0.881678 StartY=18.0885 StartZ=0 EndX=-0.881678 EndY=18.0885 EndZ=0
    g3: LineSegment StartX=-0.881678 StartY=18.0885 StartZ=0 EndX=-1.42658 EndY=16.4115 EndZ=0
    g4: LineSegment StartX=-1.42658 StartY=16.4115 StartZ=0 EndX=0 EndY=15.375 EndZ=0
    g5: Circle CenterX=0 CenterY=16.875 CenterZ=0 NormalX=0 NormalY=0 NormalZ=1 AngleXU=0 Radius=1.5
    g6: LineSegment StartX=1.42658 StartY=-16.4115 StartZ=0 EndX=0 EndY=-15.375 EndZ=0
    g7: LineSegment StartX=0 StartY=-15.375 StartZ=0 EndX=-1.42658 EndY=-16.4115 EndZ=0
    g8: LineSegment StartX=-1.42658 StartY=-16.4115 StartZ=0 EndX=-0.881678 EndY=-18.0885 EndZ=0
    g9: LineSegment StartX=-0.881678 StartY=-18.0885 StartZ=0 EndX=0.881678 EndY=-18.0885 EndZ=0
    g10: LineSegment StartX=0.881678 StartY=-18.0885 StartZ=0 EndX=1.42658 EndY=-16.4115 EndZ=0
    g11: Circle CenterX=0 CenterY=-16.875 CenterZ=0 NormalX=0 NormalY=0 NormalZ=1 AngleXU=0 Radius=1.5
  constraints (29):
    c: Coincident(g0,g1)
    c: Coincident(g1,g2)
    c: Coincident(g2,g3)
    c: Coincident(g3,g4)
    c: Coincident(g4,g0)
    c: Equal(g0, g1-g4) x4
    c: PointOnObject(g0,g5)
    c: PointOnObject(g1,g5)
    c: PointOnObject(g2,g5)
    c: PointOnObject(g3,g5)
    c: PointOnObject(g4,g5)
    c: PointOnObject(g5,g-2)
    c: Diameter(g5) = 3  'diameter'
    c: PointOnObject(g0,g-2)
    c: Coincident(g6,g7)
    c: Coincident(g7,g8)
    c: Coincident(g8,g9)
    c: Coincident(g9,g10)
    c: Coincident(g10,g6)
    c: Equal(g6, g7-g10) x4
    c: PointOnObject(g6,g11)
    c: PointOnObject(g7,g11)
    c: PointOnObject(g8,g11)
    c: PointOnObject(g9,g11)
    c: PointOnObject(g10,g11)
    c: Symmetric(g5,g11,g-1)
    c: PointOnObject(g6,g-2)
    c: DistanceY(g11,g5) = 33.75  'offset'
    c: Equal(g11,g5)
FEATURE [PartDesign::Pocket] Pocket006  label="Shelf Retention Clamp Mounting Holes"
  BaseFeature = -> Pocket004
  Direction = (0,1,2e-16)
  Length = 0
  Length2 = 5
  Placement = pos=(0,0,0) rot=(1,0,0;1.5708rad)
  Profile = -> Sketch011
  ReferenceAxis = -> Sketch011 [N_Axis]
  Type = 3
  UpToFace = -> DatumPlane014 [Plane]
FEATURE [PartDesign::CoordinateSystem] Local_CS001  label="Shelf Retention Clamp Top Mounting Hole (Body)"
  AttacherType = Attacher::AttachEngine3D
  AttachmentOffset = pos=(0,16.875,0) rot=(0,1,0;3.14159rad)
  MapMode = 5
  Placement = pos=(0,101,16.875) rot=(0,0.707107,0.707107;3.14159rad)
  Support = -> [DatumPlane004]
  expr: .AttachmentOffset.Base.y = <<Shelf Retention Clamp Mounting Holes Outer>>.Constraints.offset / 2
FEATURE [PartDesign::Body] Body  label="Rack Mount Body"
  Group = -> [DatumPlane,DatumPlane002,Sketch,Pad,Sketch002,Pocket001,DatumPlane003,DatumPlane004,Local_CS,Pocket,Sketch003,Sketch004,Sketch005,Pad001,Pocket002,Sketch006,Sketch007,DatumPlane008,DatumPlane009,Pocket003,DatumPlane010,DatumPlane011,Pocket004,DatumPlane014,Sketch011,Pocket006,Local_CS001]
  Origin = -> Origin
  Tip = -> Pocket006
COMPONENT P2 — recipe-attached ("Retention Clamp", modeled in this document).
Construction recipe (the document's own serialized feature program — sketch geometry with constraints, then the solid features built on it; lengths are millimeters unless a unit is written):

FEATURE [PartDesign::Plane] DatumPlane012  label="Retention Clamp Bottom"
  Length = 60
  MapMode = 5
  Placement = pos=(0,0,0) rot=(1,0,0;1.5708rad)
  ResizeMode = 0
  Support = -> [XZ_Plane006]
  Width = 60
FEATURE [Sketcher::SketchObject] Sketch009  label="Retention Clamp Outer"
  FullyConstrained = true
  MapMode = 5
  Placement = pos=(0,0,0) rot=(1,0,0;1.5708rad)
  Support = -> [DatumPlane012]
  expr: Constraints[7] = <<Shelf Retention Clamp Mounting Holes Outer>>.Constraints.offset
  sketch-geometry (4):
    g0: ArcOfCircle CenterX=0 CenterY=16.875 CenterZ=0 NormalX=0 NormalY=0 NormalZ=1 AngleXU=0 Radius=6 StartAngle=1.64e-14 EndAngle=3.14159
    g1: ArcOfCircle CenterX=0 CenterY=-16.875 CenterZ=0 NormalX=0 NormalY=0 NormalZ=1 AngleXU=0 Radius=6 StartAngle=3.14159 EndAngle=6.28319
    g2: LineSegment StartX=-6 StartY=16.875 StartZ=0 EndX=-6 EndY=-16.875 EndZ=0
    g3: LineSegment StartX=6 StartY=-16.875 StartZ=0 EndX=6 EndY=16.875 EndZ=0
  constraints (9):
    c: Tangent(g0,g2) = -1.5708
    c: Tangent(g2,g1) = -1.5708
    c: Tangent(g1,g3) = -1.5708
    c: Tangent(g3,g0) = -1.5708
    c: Equal(g0,g1)
    c: PointOnObject(g0,g-2)
    c: Symmetric(g0,g1,g-1)
    c: DistanceY(g1,g0) = 33.75
    c: Radius(g0) = 6
FEATURE [PartDesign::Plane] DatumPlane013  label="Retention Clamp Top"
  AttachmentOffset = pos=(0,0,2) rot=(0,0,1;0rad)
  Length = 60
  MapMode = 5
  Placement = pos=(0,-2,-4e-16) rot=(1,0,0;1.5708rad)
  ResizeMode = 0
  Support = -> [DatumPlane012]
  Width = 60
FEATURE [PartDesign::Pad] Pad003  label="Retention Clamp Volume"
  Direction = (0,-1,-2e-16)
  Length = 10
  Length2 = 10
  Placement = pos=(0,0,0) rot=(1,0,0;1.5708rad)
  Profile = -> Sketch009
  ReferenceAxis = -> Sketch009 [N_Axis]
  Type = 3
  UpToFace = -> DatumPlane013 [Plane]
FEATURE [Sketcher::SketchObject] Sketch010  label="Retention Clamp Mounting Holes Outer"
  FullyConstrained = true
  MapMode = 5
  Placement = pos=(0,-2,-4e-16) rot=(1,0,0;1.5708rad)
  Support = -> [DatumPlane013]
  expr: .Constraints.offset = <<Shelf Retention Clamp Mounting Holes Outer>>.Constraints.offset
  sketch-geometry (2):
    g0: Circle CenterX=0 CenterY=16.875 CenterZ=0 NormalX=0 NormalY=0 NormalZ=1 AngleXU=0 Radius=1.55
    g1: Circle CenterX=0 CenterY=-16.875 CenterZ=0 NormalX=0 NormalY=0 NormalZ=1 AngleXU=0 Radius=1.55
  constraints (5):
    c: PointOnObject(g0,g-2)
    c: Symmetric(g0,g1,g-1)
    c: Equal(g0,g1)
    c: Diameter(g0) = 3.1  'diameter'
    c: DistanceY(g1,g0) = 33.75  'offset'
FEATURE [PartDesign::Pocket] Pocket005  label="Retention Clamp Mounting Holes"
  BaseFeature = -> Pad003
  Direction = (0,1,2e-16)
  Length = 0
  Length2 = 5
  Placement = pos=(0,0,0) rot=(1,0,0;1.5708rad)
  Profile = -> Sketch010
  ReferenceAxis = -> Sketch010 [N_Axis]
  Type = 3
  UpToFace = -> DatumPlane012
FEATURE [PartDesign::CoordinateSystem] Local_CS002  label="Retention Clamp Top Mounting Hole (Body)"
  AttacherType = Attacher::AttachEngine3D
  AttachmentOffset = pos=(0,16.875,0) rot=(0,0,1;0rad)
  MapMode = 5
  Placement = pos=(0,-3.7e-15,16.875) rot=(1,0,0;1.5708rad)
  Support = -> [DatumPlane012]
  expr: .AttachmentOffset.Base.y = <<Shelf Retention Clamp Mounting Holes Outer>>.Constraints.offset / 2
FEATURE [PartDesign::Body] Retention_Clamp_Body  label="Retention Clamp Body"
  Group = -> [Sketch009,DatumPlane012,DatumPlane013,Pad003,Sketch010,Pocket005,Local_CS002]
  Origin = -> Origin006
  Tip = -> Pocket005
PROVENANCE & LICENSES
A FreeCAD (.FCStd) document from a public repository crawl; recipes are the document's own serialized feature recipes (and, for linked parts, companion documents' recipes).
License: as declared in the source repository (recorded in the dataset sidecar).
